# Revit family: C3-R-SD
name_source: partatom
category: Doors
revit_build: Autodesk Revit LT 2017 (Build: 20160225_1515(x64)
units: mm (PartAtom-declared; Revit-internal decimal feet)

## family parameters
Always vertical = Yes
Cut with Voids When Loaded = No
Host = Wall
OmniClass Number = 23.30.10.00
OmniClass Title = Doors
Room Calculation Point = No
Shared = No

## types (3) — shared parameters
6 Monthly = Refer to O&M Manual
Access Clearance Top = Space above top (internal side) raccomanded 750 mm (min. 350 mm)
Analytic Construction = <Nessuno>
Annually = Refer to O&M Manual
AssetType = Alluser Antitailgating High Security Portals
Battery Supply = Yes
CE Approval = Yes
Colour = PPC RAL 30% Gloss
Daily = Refer to O&M Manual
Description = Anti Tailgating High Security portal - Cylindrical Shape
Design Country = Italy
Expected Life = Subjected to regular maintenance
ExpectedLife = Subjected to regular maintenance
Feature = Anti Tailgating High Security portal - Cylindrical Shape
FireExit = Yes
Function = Interior
HandicapAccessible = Yes
HasDrive = Yes
HasPartWinding = Yes
HasProtectiveEarth = Yes
Instruction Video = https://www.youtube.com
IsCoated = Yes
IsExternal = Yes
IsGuarded  = Yes
IsLaminated = Yes
IsWired = Yes
Manufacturer = Alluser Industrie srl
Manufacturer Country = Italy
Manufacturer Website = www.alluserindustrie.com
Monthly = Refer to O&M Manual
Overall Width = 1381 mm  [stored 4.53084 ft]
PhaseAngle = 0.00°
Product Range = High Security Portals
Product URL = https://www.alluserindustrie.com
Radius = 691 mm
Rough Height = 691 mm
SelfClosing = Yes
Shape = circular
Wall Closure = By host
Weekly = Refer to O&M Manual
Width = 1381 mm  [stored 4.53084 ft]
zero-valued in all types: Access Clearance Bottom, Access Clearance Front, Access Clearance Left, Access Clearance Rear, Access Clearance Right, BeamRadiationTransmittance, ElectricMotorEfficiency, GlassThickness2, GlassThickness3, GlazingAreaFraction, Infiltration, Life Cycle Analysis, LockedRotorCurrent, MaximumPowerOutput, NominalCurrent, NominalFrequencyRange, NominalLength, NominalVoltage, Number of Poles, NumberOfPoles, Overall Length, Reflectivity, SolarHeatGainTransmittance, StartCurrentFactor, Supply Phase, ThermalTransmittance, ThermalTransmittanceSummer, ThermalTransmittanceWinter, Translucency, UsageCurrent, Voltage

## per-type parameters (varying)
| type | ElectricalDeviceNominalPower | GlassLayers | GlassThickness1 | Gross Weight | Height | IsTempered | Location of Manufacturer | Overall Height | Size(HxWxD) | SmokeStop |
| HUC STD | 35 | 1 | 11 mm  [stored 0.0360892 ft] | 730 Kg (with glass P2A UNI EN 356) | 2320 mm  [stored 7.61155 ft] | No | Italy | 2320 mm  [stored 7.61155 ft] | 2320x1381x1381 | No |
| HUC 2134 | 0 | 0 | 0 mm  [stored 0 ft] | 745 Kg (with glass P2A UNI EN 356) | 2406 mm | Yes |  | 2406 mm | 2406x1381x1381 | Yes |
| HUC 2300 | 0 | 0 | 0 mm  [stored 0 ft] | 760 Kg (with glass P2A UNI EN 356) | 2560 mm  [stored 8.39895 ft] | Yes |  | 2560 mm  [stored 8.39895 ft] | 2560x1381x1381 | Yes |

note: [stored X ft] marks values corroborated as IEEE doubles in the binary element streams (Revit-internal decimal feet)
